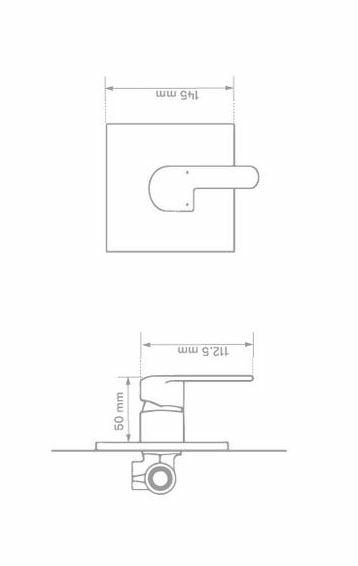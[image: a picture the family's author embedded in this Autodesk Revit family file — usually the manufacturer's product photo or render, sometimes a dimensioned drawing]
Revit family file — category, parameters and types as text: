
# Revit family: 01-0208-11 MEZCLADOR LAVAMANOS 8” PARED PORTOBELLO
name_source: partatom
category: Plumbing Fixtures
revit_build: Autodesk Revit 2018 (Build: 20170223_1515(x64)
units: mm (PartAtom-declared; Revit-internal decimal feet)

## family parameters
Cut with Voids When Loaded = No
Host = Face
OmniClass Number = 23.31.11.00
Part Type = Normal
Room Calculation Point = No
Round Connector Dimension = Use Diameter
Shared = No

## types (1)
- 01-0208-11
    Base - Aireador = 215 mm
    CW Connection = Yes
    Default Elevation = 0 mm  [stored 0 ft]
    Description = Mezclador Lavamanos
    Dim escudo = 60 mm  [stored 0.19685 ft]
    Distancia entre griferias = 203 mm
    HW Connection = Yes
    Link Ficha Tecnica = http://infotecnica.gricol.com
    Manija = 70 mm
    Manufacturer = Gricol
    Metal Laton Cromado = Metal Laton Cromado
    Mezclador = Mezclador
    Model = 01-0208-11
    Plastico - ABS Cromado = Plastico - ABS Cromado
    Product Name = MEZCLADOR LAVAMANOS 8” PARED PORTOBELLO
    Type Image = <None>
    URL = https://www.gricol.com
    Vent Connection = No
    Waste Connection = No

note: [stored X ft] marks values corroborated as IEEE doubles in the binary element streams (Revit-internal decimal feet)

## geometry (parser evidence)
native form markers: Blend x2, Sweep x12
no freeform markers — native parametric forms only
